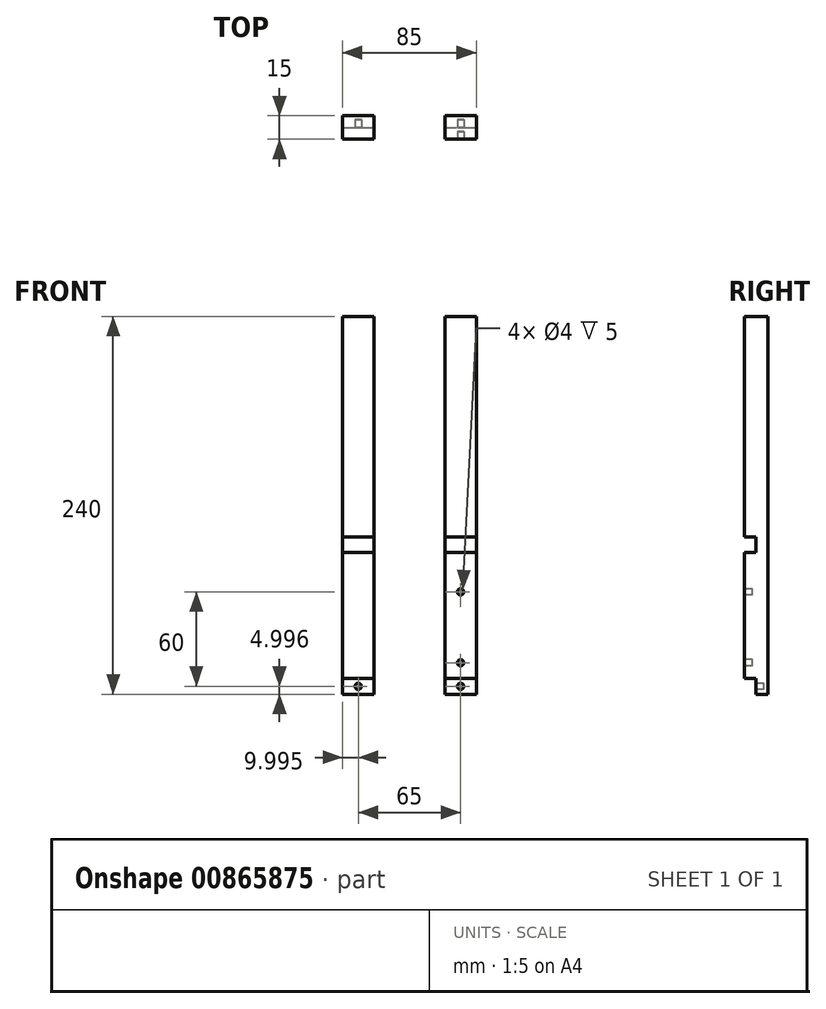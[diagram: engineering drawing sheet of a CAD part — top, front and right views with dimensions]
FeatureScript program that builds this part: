
annotation { "Feature Type Name" : "Feature", "Feature Type Description" : "" }
export const myFeature = defineFeature(function(context is Context, id is Id, definition is map)
    precondition{}
    {
        {
            var Q0;
            Q0=qCreatedBy(makeId("Front.planeOp"),FACE);
            var sketch = newSketch(context, id + "F0", { "sketchPlane" : qUnion([Q0])});
            skLineSegment(sketch, "E0.bottom", {"start": v(-38.81, 165.14) * mm, "end": v(-18.81, 165.14) * mm});
            skLineSegment(sketch, "E0.top", {"start": v(-38.81, -74.86) * mm, "end": v(-18.81, -74.86) * mm});
            skLineSegment(sketch, "E0.left", {"start": v(-38.81, 165.14) * mm, "end": v(-38.81, -74.86) * mm});
            skLineSegment(sketch, "E0.right", {"start": v(-18.81, 165.14) * mm, "end": v(-18.81, -74.86) * mm});
            skSolve(sketch);
        }
        {
            var Q0;
            Q0 = qSketchRegion(id + "F0", true);
            extrude(context, id + "F1", {"entities" : qUnion([Q0]), "depth" : 15 * mm, "offsetDistance" : 25 * mm});
        }
        {
            var Q0;
            Q0=makeQuery(id+"F1.opExtrude","CAP_FACE",FACE,{"disambiguationData":[OSD([sQuery(id+"F0.wireOp",EDGE,"E0.bottom"),sQuery(id+"F0.wireOp",EDGE,"E0.top"),sQuery(id+"F0.wireOp",EDGE,"E0.left"),sQuery(id+"F0.wireOp",EDGE,"E0.right")])],"isStart":false});
            var sketch = newSketch(context, id + "F2", { "sketchPlane" : qUnion([Q0])});
            skLineSegment(sketch, "E1.bottom", {"start": v(-38.81, -74.86) * mm, "end": v(-18.81, -74.86) * mm});
            skLineSegment(sketch, "E1.top", {"start": v(-38.81, -64.86) * mm, "end": v(-18.81, -64.86) * mm});
            skLineSegment(sketch, "E1.left", {"start": v(-38.81, -74.86) * mm, "end": v(-38.81, -64.86) * mm});
            skLineSegment(sketch, "E1.right", {"start": v(-18.81, -74.86) * mm, "end": v(-18.81, -64.86) * mm});
            skLineSegment(sketch, "E2.bottom", {"start": v(-38.81, 25.14) * mm, "end": v(-18.81, 25.14) * mm});
            skLineSegment(sketch, "E2.top", {"start": v(-38.81, 15.14) * mm, "end": v(-18.81, 15.14) * mm});
            skLineSegment(sketch, "E2.left", {"start": v(-38.81, 25.14) * mm, "end": v(-38.81, 15.14) * mm});
            skLineSegment(sketch, "E2.right", {"start": v(-18.81, 25.14) * mm, "end": v(-18.81, 15.14) * mm});
            skSolve(sketch);
        }
        {
            var Q0;
            Q0 = qSketchRegion(id + "F2", true);
            extrude(context, id + "F3", {"entities" : qUnion([Q0]), "operationType" : NewBodyOperationType.REMOVE, "oppositeDirection" : true, "depth" : 7.5 * mm, "offsetDistance" : 25 * mm});
        }
        {
            var Q0;
            Q0=makeQuery(id+"F3.boolean.opBoolean","COPY",FACE,{"derivedFrom":makeQuery(id+"F3.opExtrude","CAP_FACE",FACE,{"disambiguationData":[OSD([sQuery(id+"F2.wireOp",EDGE,"E1.bottom"),sQuery(id+"F2.wireOp",EDGE,"E1.top"),sQuery(id+"F2.wireOp",EDGE,"E1.left"),sQuery(id+"F2.wireOp",EDGE,"E1.right")])],"isStart":false})});
            var sketch = newSketch(context, id + "F4", { "sketchPlane" : qUnion([Q0])});
            skCircle(sketch, "E3", {"center": v(-28.81, -69.86) * mm, "radius": 2 * mm});
            skPoint(sketch, "E3.centerSnap0", {"position": v(-18.81, -69.86) * mm});
            skPoint(sketch, "E3.centerSnap1", {"position": v(-28.81, -74.86) * mm});
            skSolve(sketch);
        }
        {
            var Q0;
            Q0 = qSketchRegion(id + "F4", true);
            extrude(context, id + "F5", {"entities" : qUnion([Q0]), "operationType" : NewBodyOperationType.REMOVE, "oppositeDirection" : true, "depth" : 5 * mm, "offsetDistance" : 25 * mm});
        }
        {
            var Q0;
            Q0=makeQuery(id+"F1.opExtrude","SWEPT_BODY",BODY,{"disambiguationData":[OSD([sQuery(id+"F0.wireOp",EDGE,"E0.bottom"),sQuery(id+"F0.wireOp",EDGE,"E0.top"),sQuery(id+"F0.wireOp",EDGE,"E0.left"),sQuery(id+"F0.wireOp",EDGE,"E0.right")])]});
            transform(context, id + "F6", {"entities" : qUnion([Q0]), "transformType" : TransformType.TRANSLATION_3D, "dx" : 65 * mm, "dy" : 0 * mm, "dz" : 0 * mm, "makeCopy" : true});
        }
        {
            var Q0;
            {var subQ0=sQuery(id+"F0.wireOp",EDGE,"E0.left");var subQ1=sQuery(id+"F0.wireOp",EDGE,"E0.right");Q0=makeQuery(id+"F6.opPattern","COPY",FACE,{"derivedFrom":makeQuery(id+"F3.boolean.opBoolean","SPLIT",FACE,{"disambiguationData":[TD([makeQuery(id+"F3.opExtrude","SWEPT_FACE",FACE,{"disambiguationData":[OSD([sQuery(id+"F2.wireOp",EDGE,"E1.top")])]})])],"derivedFrom":makeQuery(id+"F1.opExtrude","CAP_FACE",FACE,{"disambiguationData":[OSD([sQuery(id+"F0.wireOp",EDGE,"E0.bottom"),sQuery(id+"F0.wireOp",EDGE,"E0.top"),subQ0,subQ1])],"isStart":false})}),"instanceName":"1"});}
            var sketch = newSketch(context, id + "F7", { "sketchPlane" : qUnion([Q0])});
            skCircle(sketch, "E4", {"center": v(36.19, -9.86) * mm, "radius": 2 * mm});
            skPoint(sketch, "E4.centerSnap0", {"position": v(36.19, 15.14) * mm});
            skCircle(sketch, "E5", {"center": v(36.19, -54.86) * mm, "radius": 2 * mm});
            skSolve(sketch);
        }
        {
            var Q0;
            Q0 = qSketchRegion(id + "F7", true);
            extrude(context, id + "F8", {"entities" : qUnion([Q0]), "operationType" : NewBodyOperationType.REMOVE, "oppositeDirection" : true, "depth" : 5 * mm, "offsetDistance" : 25 * mm});
        }
    });
